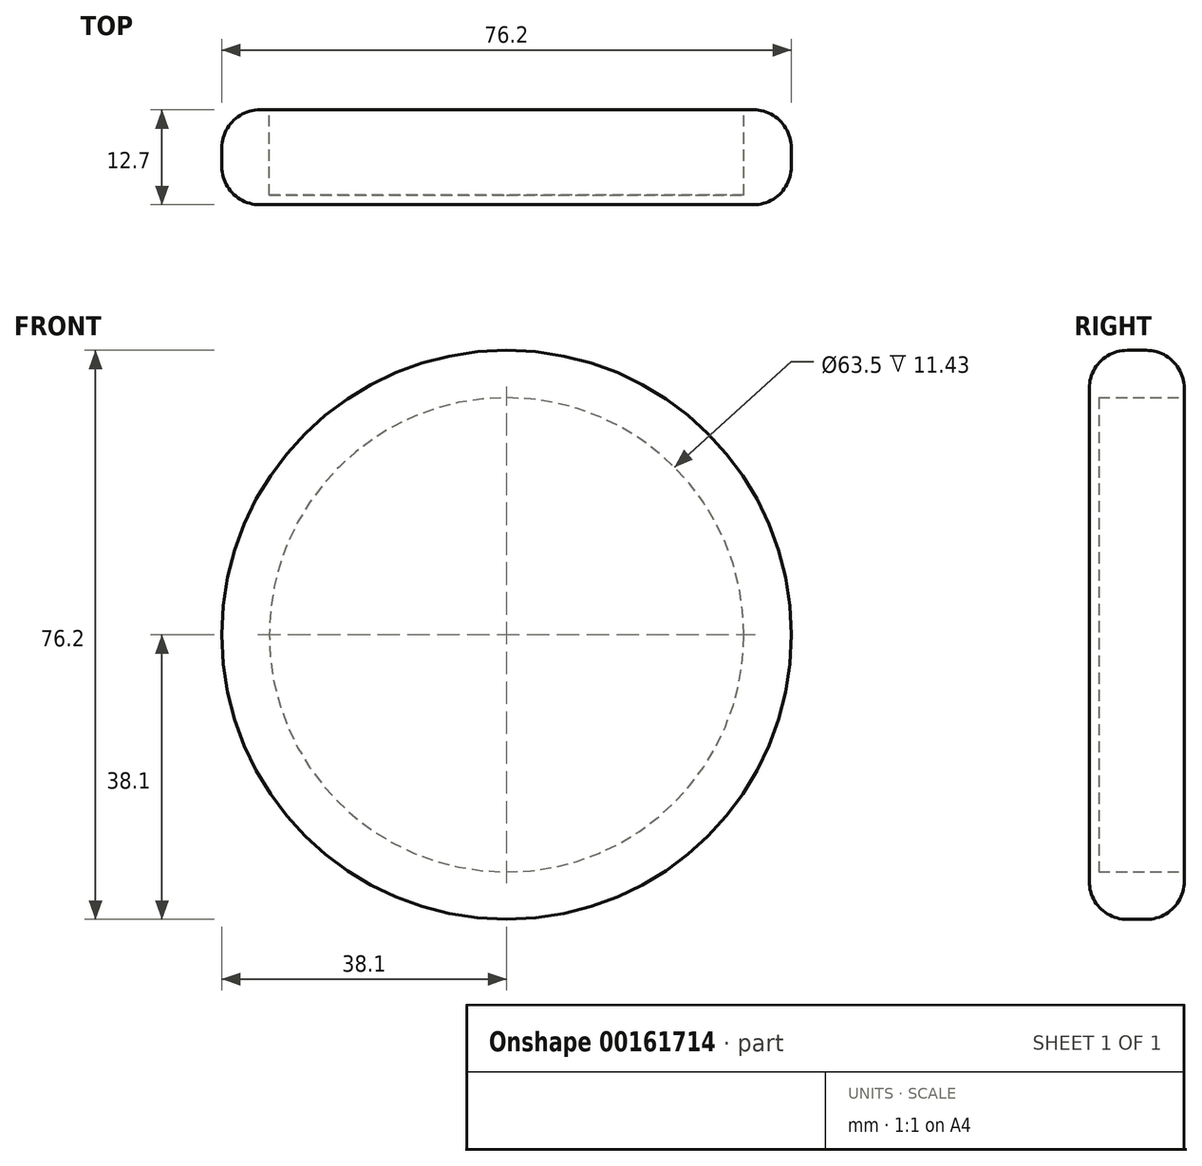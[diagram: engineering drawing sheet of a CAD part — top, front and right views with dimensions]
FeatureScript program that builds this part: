
annotation { "Feature Type Name" : "Feature", "Feature Type Description" : "" }
export const myFeature = defineFeature(function(context is Context, id is Id, definition is map)
    precondition{}
    {
        {
            var Q0;
            Q0=qCreatedBy(makeId("Front.planeOp"),FACE);
            var sketch = newSketch(context, id + "F0", { "sketchPlane" : qUnion([Q0])});
            skCircle(sketch, "E0", {"center": v(0, 0) * mm, "radius": 38.1 * mm});
            skSolve(sketch);
        }
        {
            var Q0;
            Q0 = qSketchRegion(id + "F0", true);
            extrude(context, id + "F1", {"entities" : qUnion([Q0]), "depth" : 12.7 * mm});
        }
        {
            var Q0;
            Q0=makeQuery(id+"F1.opExtrude","CAP_FACE",FACE,{"disambiguationData":[OSD([sQuery(id+"F0.wireOp",EDGE,"E0")])],"isStart":true});
            var sketch = newSketch(context, id + "F2", { "sketchPlane" : qUnion([Q0])});
            skCircle(sketch, "E1", {"center": v(0, 0) * mm, "radius": 31.75 * mm});
            skSolve(sketch);
        }
        {
            var Q0;
            Q0 = qSketchRegion(id + "F2", true);
            extrude(context, id + "F3", {"entities" : qUnion([Q0]), "operationType" : NewBodyOperationType.REMOVE, "oppositeDirection" : true, "depth" : 11.43 * mm});
        }
        {
            var Q0;
            Q0=makeQuery(id+"F1.opExtrude","SWEPT_FACE",FACE,{"disambiguationData":[OSD([sQuery(id+"F0.wireOp",EDGE,"E0")])]});
            fillet(context, id + "F4", {"entities" : qUnion([Q0]), "radius" : 5.08 * mm, "tangentPropagation" : true, "allowEdgeOverflow" : false});
        }
    });
